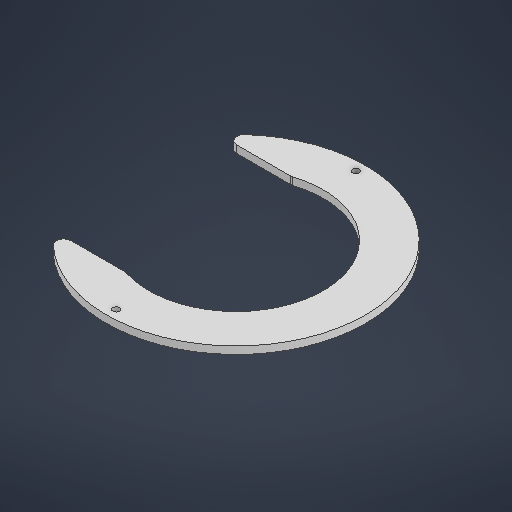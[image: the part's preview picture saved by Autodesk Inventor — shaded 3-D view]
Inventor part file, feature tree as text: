
AUTODESK INVENTOR PART (.ipt)
format: ipt  version: 2025 (Build 290162000, 162)  size: 220,672 bytes
history: native  units: in
note: dims shown in document units (in); Inventor stores cm internally (conversion verified against a paired STEP export)
features: extrude x1, fillet x1, sketch x1
ambient origin geometry x8: Origin, YZ Plane, XZ Plane, XY Plane, X Axis, Y Axis, Z Axis, Center Point
bodies: Solid1 (feature_tree)
feature tree (3):
  extrude  "Extrusion1"  Depth=0.1969in
  fillet  "Fillet1"  Radius=6.8898in
  sketch  "Sketch1"  dims[d0=4.6457in d1=6.378in d2=6.8898in d3=0.1772in d4=0.1772in d5=0.1969in d6=0.0in d7=4.4094in d9=3.1496in d10=0.3937in d11=0.1969in d12=0.1969in]
